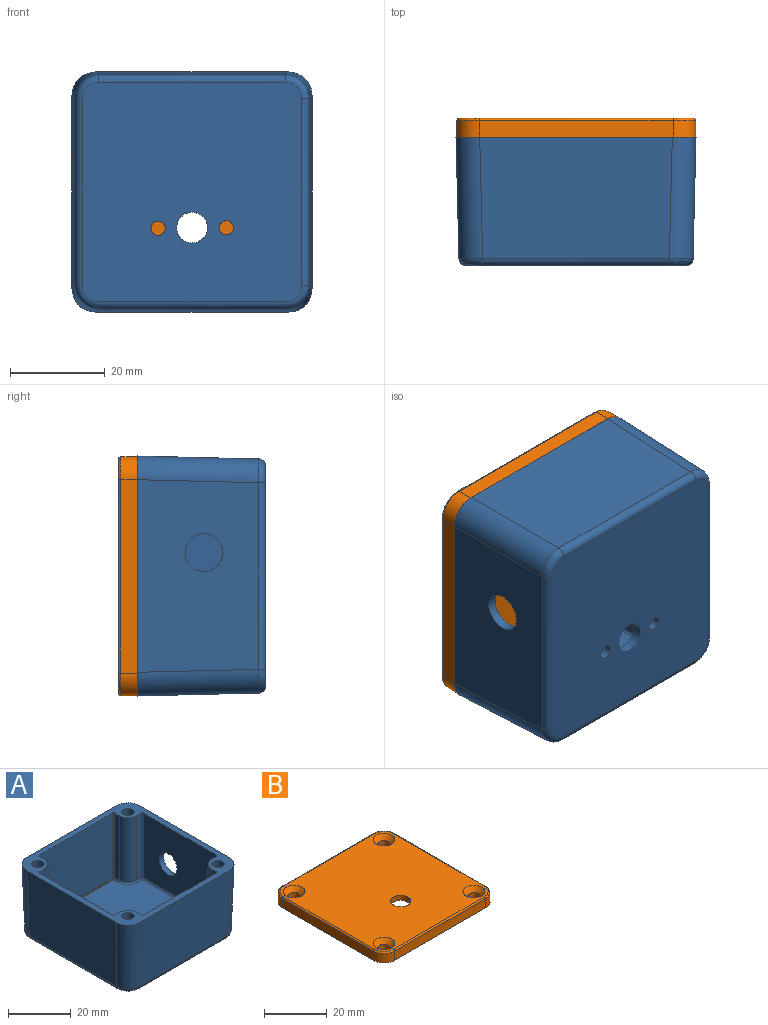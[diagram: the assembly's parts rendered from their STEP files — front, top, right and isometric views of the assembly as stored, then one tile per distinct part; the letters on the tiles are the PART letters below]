
ASSEMBLY  parts=2 mates=1
PART A: 289 faces, bbox 50.7x50.7x153.1 mm
  f0: plane 44.52x44.52mm, normal (0,0,1), area 1761.3mm2, adj f1,f69,f70,f71,f72,f73,f74,f75
  f1: cylinder r=1.5mm len=3mm, axis (0,0,1), area 18.4mm2, adj f0,f2
  f2: plane 46.36x46.36mm, normal (0,0,-1), area 2090.7mm2, adj f1,f3,f62,f63,f64,f65,f66,f67
  f3: bspline ~5x5mm, area 16.1mm2, adj f2,f4,f62,f68
  f4: cylinder r=5mm len=25.59mm, axis (-0.02,-0.02,-1), area 200.6mm2, adj f3,f5,f44,f61
  f5: plane 40.6x25.54mm, normal (1,0,-0.02), area 971mm2, adj f4,f6,f11,f44,f68
  f6: cylinder r=5mm len=25.59mm, axis (-0.02,0.02,-1), area 200.6mm2, adj f5,f7,f44,f67
  f7: plane 40.6x25.54mm, normal (0,-1,-0.02), area 1021.2mm2, adj f6,f8,f44,f66
  f8: cylinder r=5mm len=25.59mm, axis (0.02,0.02,-1), area 200.6mm2, adj f7,f9,f44,f65
  f9: plane 40.6x25.54mm, normal (-1,0,-0.02), area 1021.2mm2, adj f8,f10,f44,f64
  f10: cylinder r=5mm len=25.59mm, axis (0.02,-0.02,-1), area 200.6mm2, adj f9,f44,f61,f63
  f11: cylinder r=4mm len=8.05mm, axis (1,0,-0.02), area 49mm2, adj f5,f12
  f12: plane 32.7x24.56mm, normal (-1,0,0.02), area 739.5mm2, adj f11,f13,f42,f44,f85
  f13: cylinder r=0.5mm len=24.57mm, axis (-0.02,-0.02,-1), area 19.3mm2, adj f12,f14,f41,f44
  f14: plane 24.56x2.56mm, normal (0,-1,0.02), area 48.6mm2, adj f13,f15,f44,f84
  f15: cylinder r=4mm len=24.6mm, axis (-0.02,-0.02,-1), area 154.4mm2, adj f14,f16,f44,f83
  f16: plane 24.56x2.56mm, normal (-1,0,0.02), area 48.6mm2, adj f15,f17,f44,f82
  f17: cylinder r=0.5mm len=24.57mm, axis (0.02,0.02,1), area 19.3mm2, adj f16,f18,f40,f44
  f18: plane 32.7x24.56mm, normal (0,-1,0.02), area 789.7mm2, adj f17,f19,f44,f80
  f19: cylinder r=0.5mm len=24.57mm, axis (0.02,-0.02,-1), area 19.3mm2, adj f18,f20,f39,f44
  f20: plane 24.56x2.56mm, normal (1,0,0.02), area 48.6mm2, adj f19,f21,f44,f79
  f21: cylinder r=4mm len=24.6mm, axis (0.02,-0.02,-1), area 154.4mm2, adj f20,f22,f44,f78
  f22: plane 24.56x2.56mm, normal (0,-1,0.02), area 48.6mm2, adj f21,f23,f44,f77
  f23: cylinder r=0.5mm len=24.57mm, axis (-0.02,0.02,1), area 19.3mm2, adj f22,f24,f38,f44
  f24: plane 32.7x24.56mm, normal (1,0,0.02), area 789.7mm2, adj f23,f25,f44,f76
  f25: cylinder r=0.5mm len=24.57mm, axis (0.02,0.02,-1), area 19.3mm2, adj f24,f26,f37,f44
  f26: plane 24.56x2.56mm, normal (0,1,0.02), area 48.6mm2, adj f25,f27,f44,f75
  f27: cylinder r=4mm len=24.6mm, axis (0.02,0.02,-1), area 154.4mm2, adj f26,f28,f44,f74
  f28: plane 24.56x2.56mm, normal (1,0,0.02), area 48.6mm2, adj f27,f29,f44,f73
  f29: cylinder r=0.5mm len=24.57mm, axis (-0.02,-0.02,1), area 19.3mm2, adj f28,f30,f36,f44
  f30: plane 32.7x24.56mm, normal (0,1,0.02), area 789.7mm2, adj f29,f31,f44,f72
  f31: cylinder r=0.5mm len=24.57mm, axis (-0.02,0.02,-1), area 19.3mm2, adj f30,f32,f35,f44
  f32: plane 24.56x2.56mm, normal (-1,0,0.02), area 48.6mm2, adj f31,f33,f44,f71
  f33: cylinder r=4mm len=24.6mm, axis (-0.02,0.02,-1), area 154.4mm2, adj f32,f34,f44,f70
  f34: plane 24.56x2.56mm, normal (0,1,0.02), area 48.6mm2, adj f33,f42,f44,f69
  f35: sphere r=0.5mm, area 0.5mm2, adj f31,f71,f72
  f36: sphere r=0.5mm, area 0.4mm2, adj f29,f72,f73
  f37: sphere r=0.5mm, area 0.4mm2, adj f25,f75,f76
  f38: sphere r=0.5mm, area 0.5mm2, adj f23,f76,f77
  f39: sphere r=0.5mm, area 0.7mm2, adj f19,f79,f80
  f40: sphere r=0.5mm, area 0.1mm2, adj f17,f80,f82
  f41: sphere r=0.5mm, area 0.2mm2, adj f13,f84,f85
  f42: cylinder r=0.5mm len=24.57mm, axis (0.02,-0.02,1), area 19.3mm2, adj f12,f34,f43,f44
  f43: sphere r=0.5mm, area 0.4mm2, adj f42,f69,f85
  f44: plane 50.7x50.7mm, normal (0,0,1), area 466mm2, adj f4,f5,f6,f7,f8,f9,f10,f12
  f45: cylinder r=1.95mm len=3.9mm, axis (0,0,1), area 29.4mm2, adj f44,f46
  f46: plane 3.9x3.9mm, normal (0,0,1), area 6.5mm2, adj f45,f47
  f47: cylinder r=1.32mm len=7.6mm, axis (0,0,1), area 63.1mm2, adj f46,f48
  f48: plane 2.64x2.64mm, normal (0,0,1), area 5.5mm2, adj f47
  f49: cylinder r=1.95mm len=3.9mm, axis (0,0,1), area 29.4mm2, adj f44,f50
  f50: plane 3.9x3.9mm, normal (0,0,1), area 6.5mm2, adj f49,f51
  f51: cylinder r=1.32mm len=7.6mm, axis (0,0,1), area 63.1mm2, adj f50,f52
  f52: plane 2.64x2.64mm, normal (0,0,1), area 5.5mm2, adj f51
  f53: cylinder r=1.95mm len=3.9mm, axis (0,0,1), area 29.4mm2, adj f44,f54
  f54: plane 3.9x3.9mm, normal (0,0,1), area 6.5mm2, adj f53,f55
  f55: cylinder r=1.32mm len=7.6mm, axis (0,0,1), area 63.1mm2, adj f54,f56
  f56: plane 2.64x2.64mm, normal (0,0,1), area 5.5mm2, adj f55
  f57: cylinder r=1.95mm len=3.9mm, axis (0,0,1), area 29.4mm2, adj f44,f58
  f58: plane 3.9x3.9mm, normal (0,0,1), area 6.5mm2, adj f57,f59
  f59: cylinder r=1.32mm len=7.6mm, axis (0,0,1), area 63.1mm2, adj f58,f60
  f60: plane 2.64x2.64mm, normal (0,0,1), area 5.5mm2, adj f59
  f61: plane 40.6x25.54mm, normal (0,1,-0.02), area 1021.2mm2, adj f4,f10,f44,f62
  f62: cylinder r=1.5mm len=39.35mm, axis (-1,0,0), area 91.3mm2, adj f2,f3,f61,f63
  f63: bspline ~5x5mm, area 16.1mm2, adj f2,f10,f62,f64
  f64: cylinder r=1.5mm len=39.35mm, axis (0,-1,0), area 91.3mm2, adj f2,f9,f63,f65
  f65: bspline ~5x5mm, area 16.1mm2, adj f2,f8,f64,f66
  f66: cylinder r=1.5mm len=39.35mm, axis (1,0,0), area 91.3mm2, adj f2,f7,f65,f67
  f67: bspline ~5x5mm, area 16.1mm2, adj f2,f6,f66,f68
  f68: cylinder r=1.5mm len=39.35mm, axis (0,1,0), area 91.3mm2, adj f2,f3,f5,f67
  f69: cylinder r=0.5mm len=1.96mm, axis (1,0,0), area 1.5mm2, adj f0,f34,f43,f70
  f70: bspline ~4.5x4.5mm, area 5.1mm2, adj f0,f33,f69,f71
  f71: cylinder r=0.5mm len=1.96mm, axis (0,1,0), area 1.5mm2, adj f0,f32,f35,f70
  f72: cylinder r=0.5mm len=31.59mm, axis (-1,0,0), area 24.4mm2, adj f0,f30,f35,f36
  f73: cylinder r=0.5mm len=1.96mm, axis (0,-1,0), area 1.5mm2, adj f0,f28,f36,f74
  f74: bspline ~4.5x4.5mm, area 5.1mm2, adj f0,f27,f73,f75
  f75: cylinder r=0.5mm len=1.96mm, axis (1,0,0), area 1.5mm2, adj f0,f26,f37,f74
  f76: cylinder r=0.5mm len=31.59mm, axis (0,1,0), area 24.4mm2, adj f0,f24,f37,f38
  f77: cylinder r=0.5mm len=1.96mm, axis (-1,0,0), area 1.5mm2, adj f0,f22,f38,f78
  f78: bspline ~4.5x4.5mm, area 5.1mm2, adj f0,f21,f77,f79
  f79: cylinder r=0.5mm len=1.96mm, axis (0,-1,0), area 1.5mm2, adj f0,f20,f39,f78
  f80: cylinder r=0.5mm len=31.59mm, axis (1,0,0), area 24.4mm2, adj f0,f18,f39,f40,f81
  f81: sphere r=0.5mm, area 0mm2, adj f80,f82
  f82: cylinder r=0.5mm len=1.96mm, axis (0,1,0), area 1.5mm2, adj f0,f16,f40,f81,f83
  f83: bspline ~4.5x4.5mm, area 5.1mm2, adj f0,f15,f82,f84
  f84: cylinder r=0.5mm len=1.96mm, axis (-1,0,0), area 1.5mm2, adj f0,f14,f41,f83
  f85: cylinder r=0.5mm len=31.59mm, axis (0,-1,0), area 24.4mm2, adj f0,f12,f41,f43
  f86: plane 0.89x0.2mm, normal (0,1,0), area 0.2mm2, adj f0,f87,f88,f92
  f87: plane 2x1.16mm, normal (0,0,1), area 0.7mm2, adj f86,f88,f89,f90,f91,f92
  f88: plane 1.76x0.2mm, normal (1,0,0), area 0.4mm2, adj f0,f86,f87,f89
  f89: plane 0.27x0.2mm, normal (0,1,0), area 0.1mm2, adj f0,f87,f88,f90
  f90: plane 2x0.2mm, normal (-1,0,0), area 0.4mm2, adj f0,f87,f89,f91
  f91: plane 1.16x0.2mm, normal (0,-1,0), area 0.2mm2, adj f0,f87,f90,f92
  f92: plane 0.24x0.2mm, normal (1,0,0), area 0mm2, adj f0,f86,f87,f91
  f93: bspline ~152.98x1.04mm, area 0.3mm2, adj f0,f94,f104,f106
  f94: plane 2.08x1.28mm, normal (0,0,1), area 1.2mm2, adj f93,f95,f97,f98,f99,f100,f101,f102
  f95: bspline ~152.98x0.61mm, area 0.1mm2, adj f94,f96,f97,f103
  f96: plane 1.64x0.73mm, normal (0,0,1), area 1mm2, adj f95,f97,f98,f99,f100,f101,f102,f103
  f97: bspline ~152.98x0.61mm, area 0.1mm2, adj f94,f95,f96,f98
  f98: bspline ~152.98x0.29mm, area 0.1mm2, adj f94,f96,f97,f99
  f99: bspline ~152.98x0.3mm, area 0.1mm2, adj f94,f96,f98,f100
  f100: bspline ~152.98x0.61mm, area 0.1mm2, adj f94,f96,f99,f101
  f101: bspline ~152.98x0.6mm, area 0.1mm2, adj f94,f96,f100,f102
  f102: bspline ~152.98x0.3mm, area 0.1mm2, adj f94,f96,f101,f103
  f103: bspline ~152.98x0.3mm, area 0.1mm2, adj f94,f95,f96,f102
  f104: bspline ~152.98x1.04mm, area 0.3mm2, adj f0,f93,f94,f105
  f105: bspline ~152.98x1.04mm, area 0.3mm2, adj f0,f94,f104,f106
  f106: bspline ~152.98x1.04mm, area 0.3mm2, adj f0,f93,f94,f105
  f107: plane 0.2x0.01mm, normal (0,1,0), area 0mm2, adj f0,f108,f117,f129
  f108: plane 2.08x1.3mm, normal (0,0,1), area 1.2mm2, adj f107,f109,f111,f112,f113,f114,f115,f116
  f109: bspline ~152.98x0.53mm, area 0.1mm2, adj f108,f110,f111,f116
  f110: plane 0.88x0.75mm, normal (0,0,1), area 0.5mm2, adj f109,f111,f112,f113,f114,f115,f116
  f111: bspline ~152.98x0.25mm, area 0.1mm2, adj f108,f109,f110,f112
  f112: bspline ~152.98x0.46mm, area 0.1mm2, adj f108,f110,f111,f113
  f113: bspline ~152.98x0.35mm, area 0.1mm2, adj f108,f110,f112,f114
  f114: bspline ~152.98x0.25mm, area 0.1mm2, adj f108,f110,f113,f115
  f115: bspline ~152.98x0.36mm, area 0.1mm2, adj f108,f110,f114,f116
  f116: bspline ~152.98x0.13mm, area 0mm2, adj f108,f109,f110,f115
  f117: plane 0.26x0.2mm, normal (-1,0,0), area 0.1mm2, adj f0,f107,f108,f118
  f118: bspline ~152.98x0.23mm, area 0mm2, adj f0,f108,f117,f119
  f119: bspline ~152.98x0.68mm, area 0.2mm2, adj f0,f108,f118,f120
  f120: bspline ~152.98x0.84mm, area 0.2mm2, adj f0,f108,f119,f121
  f121: bspline ~152.98x0.74mm, area 0.2mm2, adj f0,f108,f120,f122
  f122: bspline ~152.98x0.44mm, area 0.1mm2, adj f0,f108,f121,f123
  f123: bspline ~152.98x0.45mm, area 0.1mm2, adj f0,f108,f122,f124
  f124: bspline ~152.98x0.5mm, area 0.1mm2, adj f0,f108,f123,f125
  f125: bspline ~152.98x0.51mm, area 0.1mm2, adj f0,f108,f124,f126
  f126: bspline ~152.98x0.39mm, area 0.1mm2, adj f0,f108,f125,f127
  f127: bspline ~152.98x0.42mm, area 0.1mm2, adj f0,f108,f126,f128
  f128: bspline ~152.98x0.67mm, area 0.2mm2, adj f0,f108,f127,f129
  f129: bspline ~152.98x0.25mm, area 0.1mm2, adj f0,f107,f108,f128
  f130: bspline ~152.98x0.4mm, area 0.1mm2, adj f0,f131,f132,f150
  f131: plane 2.04x1.19mm, normal (0,0,1), area 1.1mm2, adj f130,f132,f133,f134,f135,f136,f137,f138
  f132: bspline ~152.98x0.33mm, area 0.1mm2, adj f0,f130,f131,f133
  f133: bspline ~152.98x0.29mm, area 0.1mm2, adj f0,f131,f132,f134
  f134: bspline ~152.98x0.33mm, area 0.1mm2, adj f0,f131,f133,f135
  f135: bspline ~152.98x0.29mm, area 0.1mm2, adj f0,f131,f134,f136
  f136: bspline ~152.98x0.29mm, area 0.1mm2, adj f0,f131,f135,f137
  f137: bspline ~152.98x0.22mm, area 0mm2, adj f0,f131,f136,f138
  f138: plane 0.2x0.02mm, normal (0,1,0), area 0mm2, adj f0,f131,f137,f139
  f139: plane 0.28x0.2mm, normal (-1,0,0), area 0.1mm2, adj f0,f131,f138,f140
  f140: bspline ~152.98x0.52mm, area 0.1mm2, adj f0,f131,f139,f141
  f141: bspline ~152.98x0.49mm, area 0.1mm2, adj f0,f131,f140,f142
  f142: bspline ~152.98x0.48mm, area 0.1mm2, adj f0,f131,f141,f143
  f143: bspline ~152.98x0.48mm, area 0.1mm2, adj f0,f131,f142,f144
  f144: bspline ~152.98x0.46mm, area 0.1mm2, adj f0,f131,f143,f145
  f145: bspline ~152.98x0.18mm, area 0mm2, adj f0,f131,f144,f146
  f146: plane 0.53x0.2mm, normal (1,0,0), area 0.1mm2, adj f0,f131,f145,f147
  f147: plane 0.84x0.2mm, normal (0,-1,0), area 0.2mm2, adj f0,f131,f146,f148
  f148: plane 0.24x0.2mm, normal (1,0,0), area 0mm2, adj f0,f131,f147,f149
  f149: plane 1.1x0.2mm, normal (0,1,0), area 0.2mm2, adj f0,f131,f148,f150
  f150: plane 1.03x0.2mm, normal (-1,0,0), area 0.2mm2, adj f0,f130,f131,f149
  f151: bspline ~152.98x0.41mm, area 0.1mm2, adj f0,f152,f153,f162
  f152: plane 2.01x0.98mm, normal (0,0,1), area 0.7mm2, adj f151,f153,f154,f155,f156,f157,f158,f159
  f153: plane 0.2x0.18mm, normal (-1,0,0), area 0mm2, adj f0,f151,f152,f154
  f154: plane 0.36x0.2mm, normal (0,-1,0), area 0.1mm2, adj f0,f152,f153,f155
  f155: plane 1.34x0.2mm, normal (-1,0,0), area 0.3mm2, adj f0,f152,f154,f156
  f156: plane 0.36x0.2mm, normal (0,1,0), area 0.1mm2, adj f0,f152,f155,f157
  f157: plane 0.2x0.2mm, normal (-1,0,0), area 0mm2, adj f0,f152,f156,f158
  f158: plane 0.98x0.2mm, normal (0,-1,0), area 0.2mm2, adj f0,f152,f157,f159
  f159: plane 0.2x0.2mm, normal (1,0,0), area 0mm2, adj f0,f152,f158,f160
  f160: plane 0.36x0.2mm, normal (0,1,0), area 0.1mm2, adj f0,f152,f159,f161
  f161: plane 1.8x0.2mm, normal (1,0,0), area 0.4mm2, adj f0,f152,f160,f162
  f162: plane 0.21x0.2mm, normal (0,1,0), area 0mm2, adj f0,f151,f152,f161
  f163: plane 0.46x0.2mm, normal (0,1,0), area 0.1mm2, adj f0,f164,f173,f178
  f164: plane 2x1.58mm, normal (0,0,1), area 1.4mm2, adj f163,f165,f167,f168,f169,f170,f171,f172
  f165: bspline ~152.98x0.65mm, area 0.2mm2, adj f164,f166,f167,f172
  f166: plane 1.54x1.03mm, normal (0,0,1), area 1.4mm2, adj f165,f167,f168,f169,f170,f171,f172
  f167: bspline ~152.98x0.53mm, area 0.1mm2, adj f164,f165,f166,f168
  f168: plane 0.2x0.2mm, normal (0,-1,0), area 0mm2, adj f164,f166,f167,f169
  f169: plane 1.54x0.2mm, normal (1,0,0), area 0.3mm2, adj f164,f166,f168,f170
  f170: plane 0.2x0.2mm, normal (0,1,0), area 0mm2, adj f164,f166,f169,f171
  f171: bspline ~152.98x0.55mm, area 0.1mm2, adj f164,f166,f170,f172
  f172: bspline ~152.98x0.64mm, area 0.1mm2, adj f164,f165,f166,f171
  f173: plane 2x0.2mm, normal (-1,0,0), area 0.4mm2, adj f0,f163,f164,f174
  f174: plane 0.46x0.2mm, normal (0,-1,0), area 0.1mm2, adj f0,f164,f173,f175
  f175: bspline ~152.98x0.71mm, area 0.1mm2, adj f0,f164,f174,f176
  f176: bspline ~152.98x0.84mm, area 0.2mm2, adj f0,f164,f175,f177
  f177: bspline ~152.98x0.84mm, area 0.2mm2, adj f0,f164,f176,f178
  f178: bspline ~152.98x0.72mm, area 0.1mm2, adj f0,f163,f164,f177
  f179: plane 1.58x0.81mm, normal (0.89,0.45,0), area 0.4mm2, adj f0,f180,f181,f189
  f180: plane 2x1.43mm, normal (0,0,1), area 1.5mm2, adj f179,f181,f182,f183,f184,f185,f186,f187
  f181: plane 0.38x0.2mm, normal (0,1,0), area 0.1mm2, adj f0,f179,f180,f182
  f182: plane 2x0.2mm, normal (-1,0,0), area 0.4mm2, adj f0,f180,f181,f183
  f183: plane 0.25x0.2mm, normal (0,-1,0), area 0mm2, adj f0,f180,f182,f184
  f184: plane 1.72x0.2mm, normal (1,0,0), area 0.3mm2, adj f0,f180,f183,f185
  f185: plane 1.72x0.89mm, normal (-0.89,-0.46,0), area 0.4mm2, adj f0,f180,f184,f186
  f186: plane 0.3x0.2mm, normal (0,-1,0), area 0.1mm2, adj f0,f180,f185,f187
  f187: plane 2x0.2mm, normal (1,0,0), area 0.4mm2, adj f0,f180,f186,f188
  f188: plane 0.25x0.2mm, normal (0,1,0), area 0mm2, adj f0,f180,f187,f189
  f189: plane 1.58x0.2mm, normal (-1,0,0), area 0.3mm2, adj f0,f179,f180,f188
  f190: bspline ~152.98x0.77mm, area 0.2mm2, adj f0,f191,f199,f205
  f191: plane 2.08x1.77mm, normal (0,0,1), area 1.4mm2, adj f190,f192,f194,f195,f196,f197,f198,f199
  f192: bspline ~152.98x0.6mm, area 0.1mm2, adj f191,f193,f194,f198
  f193: plane 1.62x1.21mm, normal (0,0,1), area 1.6mm2, adj f192,f194,f195,f196,f197,f198
  f194: bspline ~152.98x0.44mm, area 0.1mm2, adj f191,f192,f193,f195
  f195: bspline ~152.98x0.44mm, area 0.1mm2, adj f191,f193,f194,f196
  f196: bspline ~152.98x0.6mm, area 0.1mm2, adj f191,f193,f195,f197
  f197: bspline ~152.98x0.81mm, area 0.2mm2, adj f191,f193,f196,f198
  f198: bspline ~152.98x0.81mm, area 0.2mm2, adj f191,f192,f193,f197
  f199: bspline ~152.98x0.77mm, area 0.2mm2, adj f0,f190,f191,f200
  f200: bspline ~152.98x0.65mm, area 0.1mm2, adj f0,f191,f199,f201
  f201: bspline ~152.98x0.65mm, area 0.1mm2, adj f0,f191,f200,f202
  f202: bspline ~152.98x0.77mm, area 0.2mm2, adj f0,f191,f201,f203
  f203: bspline ~152.98x0.77mm, area 0.2mm2, adj f0,f191,f202,f204
  f204: bspline ~152.98x0.65mm, area 0.1mm2, adj f0,f191,f203,f205
  f205: bspline ~152.98x0.64mm, area 0.1mm2, adj f0,f190,f191,f204
  f206: plane 2x0.2mm, normal (-1,0,0), area 0.4mm2, adj f0,f207,f208,f219
  f207: plane 2x1.71mm, normal (0,0,1), area 1.6mm2, adj f206,f208,f209,f210,f211,f212,f213,f214
  f208: plane 0.25x0.2mm, normal (0,-1,0), area 0mm2, adj f0,f206,f207,f209
  f209: plane 1.72x0.2mm, normal (1,0,0), area 0.3mm2, adj f0,f207,f208,f210
  f210: plane 1.17x0.52mm, normal (-0.91,-0.4,0), area 0.3mm2, adj f0,f207,f209,f211
  f211: plane 0.2x0.16mm, normal (0,-1,0), area 0mm2, adj f0,f207,f210,f212
  f212: plane 1.17x0.52mm, normal (0.91,-0.41,0), area 0.3mm2, adj f0,f207,f211,f213
  f213: plane 1.72x0.2mm, normal (-1,0,0), area 0.3mm2, adj f0,f207,f212,f214
  f214: plane 0.27x0.2mm, normal (0,-1,0), area 0.1mm2, adj f0,f207,f213,f215
  f215: plane 2x0.2mm, normal (1,0,0), area 0.4mm2, adj f0,f207,f214,f216
  f216: plane 0.37x0.2mm, normal (0,1,0), area 0.1mm2, adj f0,f207,f215,f217
  f217: plane 1.11x0.48mm, normal (-0.92,0.4,0), area 0.2mm2, adj f0,f207,f216,f218
  f218: plane 1.11x0.5mm, normal (0.91,0.41,0), area 0.2mm2, adj f0,f207,f217,f219
  f219: plane 0.36x0.2mm, normal (0,1,0), area 0.1mm2, adj f0,f206,f207,f218
  f220: plane 2x0.2mm, normal (-1,0,0), area 0.4mm2, adj f0,f221,f222,f233
  f221: plane 2x1.71mm, normal (0,0,1), area 1.6mm2, adj f220,f222,f223,f224,f225,f226,f227,f228
  f222: plane 0.25x0.2mm, normal (0,-1,0), area 0mm2, adj f0,f220,f221,f223
  f223: plane 1.72x0.2mm, normal (1,0,0), area 0.3mm2, adj f0,f221,f222,f224
  f224: plane 1.17x0.52mm, normal (-0.91,-0.4,0), area 0.3mm2, adj f0,f221,f223,f225
  f225: plane 0.2x0.16mm, normal (0,-1,0), area 0mm2, adj f0,f221,f224,f226
  f226: plane 1.17x0.52mm, normal (0.91,-0.41,0), area 0.3mm2, adj f0,f221,f225,f227
  f227: plane 1.72x0.2mm, normal (-1,0,0), area 0.3mm2, adj f0,f221,f226,f228
  f228: plane 0.27x0.2mm, normal (0,-1,0), area 0.1mm2, adj f0,f221,f227,f229
  f229: plane 2x0.2mm, normal (1,0,0), area 0.4mm2, adj f0,f221,f228,f230
  f230: plane 0.37x0.2mm, normal (0,1,0), area 0.1mm2, adj f0,f221,f229,f231
  f231: plane 1.11x0.48mm, normal (-0.92,0.4,0), area 0.2mm2, adj f0,f221,f230,f232
  f232: plane 1.11x0.5mm, normal (0.91,0.41,0), area 0.2mm2, adj f0,f221,f231,f233
  f233: plane 0.36x0.2mm, normal (0,1,0), area 0.1mm2, adj f0,f220,f221,f232
  f234: plane 0.76x0.2mm, normal (0,-1,0), area 0.2mm2, adj f0,f235,f240,f246
  f235: plane 2x1.68mm, normal (0,0,1), area 1.2mm2, adj f234,f236,f238,f239,f240,f241,f242,f243
  f236: plane 0.94x0.31mm, normal (-0.95,-0.31,0), area 0.2mm2, adj f235,f237,f238,f239
  f237: plane 0.94x0.62mm, normal (0,0,1), area 0.3mm2, adj f236,f238,f239
  f238: plane 0.94x0.31mm, normal (0.95,-0.31,0), area 0.2mm2, adj f235,f236,f237,f239
  f239: plane 0.62x0.2mm, normal (0,1,0), area 0.1mm2, adj f235,f236,f237,f238
  f240: plane 0.56x0.2mm, normal (-0.95,-0.31,0), area 0.1mm2, adj f0,f234,f235,f241
  f241: plane 0.28x0.2mm, normal (0,-1,0), area 0.1mm2, adj f0,f235,f240,f242
  f242: plane 2x0.67mm, normal (0.95,0.32,0), area 0.4mm2, adj f0,f235,f241,f243
  f243: plane 0.33x0.2mm, normal (0,1,0), area 0.1mm2, adj f0,f235,f242,f244
  f244: plane 2x0.67mm, normal (-0.95,0.32,0), area 0.4mm2, adj f0,f235,f243,f245
  f245: plane 0.27x0.2mm, normal (0,-1,0), area 0.1mm2, adj f0,f235,f244,f246
  f246: plane 0.56x0.2mm, normal (0.95,-0.31,0), area 0.1mm2, adj f0,f234,f235,f245
  f247: plane 0.78x0.2mm, normal (1,0,0), area 0.2mm2, adj f0,f248,f249,f259
  f248: plane 2x1.45mm, normal (0,0,1), area 1.3mm2, adj f247,f249,f250,f251,f252,f253,f254,f255
  f249: plane 0.27x0.2mm, normal (0,1,0), area 0.1mm2, adj f0,f247,f248,f250
  f250: plane 2x0.2mm, normal (-1,0,0), area 0.4mm2, adj f0,f248,f249,f251
  f251: plane 0.27x0.2mm, normal (0,-1,0), area 0.1mm2, adj f0,f248,f250,f252
  f252: plane 0.98x0.2mm, normal (1,0,0), area 0.2mm2, adj f0,f248,f251,f253
  f253: plane 0.92x0.2mm, normal (0,-1,0), area 0.2mm2, adj f0,f248,f252,f254
  f254: plane 0.98x0.2mm, normal (-1,0,0), area 0.2mm2, adj f0,f248,f253,f255
  f255: plane 0.27x0.2mm, normal (0,-1,0), area 0.1mm2, adj f0,f248,f254,f256
  f256: plane 2x0.2mm, normal (1,0,0), area 0.4mm2, adj f0,f248,f255,f257
  f257: plane 0.27x0.2mm, normal (0,1,0), area 0.1mm2, adj f0,f248,f256,f258
  f258: plane 0.78x0.2mm, normal (-1,0,0), area 0.2mm2, adj f0,f248,f257,f259
  f259: plane 0.92x0.2mm, normal (0,1,0), area 0.2mm2, adj f0,f247,f248,f258
  f260: bspline ~152.98x0.37mm, area 0.1mm2, adj f0,f261,f278,f286
  f261: plane 2x1.36mm, normal (0,0,1), area 1.5mm2, adj f260,f262,f264,f265,f266,f267,f268,f269
  f262: bspline ~152.98x0.31mm, area 0.1mm2, adj f261,f263,f264,f269
  f263: plane 0.81x0.74mm, normal (0,0,1), area 0.5mm2, adj f262,f264,f265,f266,f267,f268,f269
  f264: bspline ~152.98x0.35mm, area 0.1mm2, adj f261,f262,f263,f265
  f265: plane 0.3x0.2mm, normal (0,-1,0), area 0.1mm2, adj f261,f263,f264,f266
  f266: plane 0.74x0.2mm, normal (1,0,0), area 0.1mm2, adj f261,f263,f265,f267
  f267: plane 0.22x0.2mm, normal (0,1,0), area 0mm2, adj f261,f263,f266,f268
  f268: bspline ~152.98x0.45mm, area 0.1mm2, adj f261,f263,f267,f269
  f269: bspline ~152.98x0.29mm, area 0.1mm2, adj f261,f262,f263,f268
  f270: bspline ~152.98x0.21mm, area 0mm2, adj f261,f271,f272,f277
  f271: plane 0.72x0.59mm, normal (0,0,1), area 0.4mm2, adj f270,f272,f273,f274,f275,f276,f277
  f272: bspline ~152.98x0.36mm, area 0.1mm2, adj f261,f270,f271,f273
  f273: plane 0.25x0.2mm, normal (0,-1,0), area 0.1mm2, adj f261,f271,f272,f274
  f274: plane 0.59x0.2mm, normal (1,0,0), area 0.1mm2, adj f261,f271,f273,f275
  f275: plane 0.3x0.2mm, normal (0,1,0), area 0.1mm2, adj f261,f271,f274,f276
  f276: bspline ~152.98x0.31mm, area 0.1mm2, adj f261,f271,f275,f277
  f277: bspline ~152.98x0.26mm, area 0.1mm2, adj f261,f270,f271,f276
  f278: bspline ~152.98x0.53mm, area 0.1mm2, adj f0,f260,f261,f279
  f279: plane 0.53x0.2mm, normal (0,1,0), area 0.1mm2, adj f0,f261,f278,f280
  f280: plane 2x0.2mm, normal (-1,0,0), area 0.4mm2, adj f0,f261,f279,f281
  f281: plane 0.57x0.2mm, normal (0,-1,0), area 0.1mm2, adj f0,f261,f280,f282
  f282: bspline ~152.98x0.58mm, area 0.1mm2, adj f0,f261,f281,f283
  f283: bspline ~152.98x0.45mm, area 0.1mm2, adj f0,f261,f282,f284
  f284: bspline ~152.98x0.5mm, area 0.1mm2, adj f0,f261,f283,f285
  f285: plane 0.2x0.01mm, normal (1,0,0), area 0mm2, adj f0,f261,f284,f286
  f286: bspline ~152.98x0.43mm, area 0.1mm2, adj f0,f260,f261,f285
  f287: cylinder r=3.25mm len=6.5mm, axis (0,0,1), area 39.8mm2, adj f0,f2
  f288: cylinder r=1.5mm len=3mm, axis (0,0,1), area 18.4mm2, adj f0,f2
PART B: 77 faces, bbox 50.6x50.6x6.1 mm
  f0: cylinder r=0.4mm len=27.5mm, axis (-1,0,0), area 17mm2, adj f1,f15,f23,f24
  f1: torus R=0.62mm, axis (0,0,-1), area 0.8mm2, adj f0,f2,f22,f24
  f2: torus R=5.88mm, axis (0,0,1), area 5.5mm2, adj f1,f3,f21,f24
  f3: torus R=0.62mm, axis (0,0,-1), area 0.8mm2, adj f2,f4,f20,f24
  f4: cylinder r=0.4mm len=27.5mm, axis (0,1,0), area 17mm2, adj f3,f5,f19,f24
  f5: torus R=0.62mm, axis (0,0,-1), area 0.8mm2, adj f4,f6,f18,f24
  f6: torus R=5.88mm, axis (0,0,1), area 5.5mm2, adj f5,f7,f17,f24
  f7: torus R=0.62mm, axis (0,0,-1), area 0.8mm2, adj f6,f8,f16,f24
  f8: cylinder r=0.4mm len=27.5mm, axis (1,0,0), area 17mm2, adj f7,f9,f24,f55
  f9: torus R=0.62mm, axis (0,0,-1), area 0.8mm2, adj f8,f10,f24,f48
  f10: torus R=5.88mm, axis (0,0,1), area 5.5mm2, adj f9,f11,f24,f49
  f11: torus R=0.62mm, axis (0,0,-1), area 0.8mm2, adj f10,f12,f24,f50
  f12: cylinder r=0.4mm len=27.5mm, axis (0,-1,0), area 17mm2, adj f11,f13,f24,f51
  f13: torus R=0.62mm, axis (0,0,-1), area 0.8mm2, adj f12,f14,f24,f52
  f14: torus R=5.88mm, axis (0,0,1), area 5.5mm2, adj f13,f15,f24,f53
  f15: torus R=0.62mm, axis (0,0,-1), area 0.8mm2, adj f0,f14,f24,f54
  f16: cone r=1.1mm half-angle=1.3deg, axis (0,0,-1), area 6mm2, adj f7,f17,f55,f72
  f17: cone r=5.4mm half-angle=1.3deg, axis (0,0,1), area 30.9mm2, adj f6,f16,f18,f72
  f18: cone r=1.1mm half-angle=1.3deg, axis (0,0,-1), area 6mm2, adj f5,f17,f19,f72
  f19: plane 27.5x3.61mm, normal (1,0,-0.02), area 99.3mm2, adj f4,f18,f20,f72
  f20: cone r=1.1mm half-angle=1.3deg, axis (0,0,-1), area 6mm2, adj f3,f19,f21,f72
  f21: cone r=5.4mm half-angle=1.3deg, axis (0,0,1), area 30.9mm2, adj f2,f20,f22,f72
  f22: cone r=1.1mm half-angle=1.3deg, axis (0,0,-1), area 6mm2, adj f1,f21,f23,f72
  f23: plane 27.5x3.61mm, normal (0,1,-0.02), area 99.3mm2, adj f0,f22,f54,f72
  f24: plane 41.74x41.74mm, normal (0,0,-1), area 1568.8mm2, adj f0,f1,f2,f3,f4,f5,f6,f7
  f25: cone r=2.73mm half-angle=41deg, axis (0,0,1), area 40.5mm2, adj f26,f47
  f26: cylinder r=1.95mm len=3.9mm, axis (0,0,1), area 27.2mm2, adj f25,f75
  f27: cone r=2.73mm half-angle=41deg, axis (0,0,1), area 40.5mm2, adj f28,f47
  f28: cylinder r=1.95mm len=3.9mm, axis (0,0,1), area 27.2mm2, adj f27,f75
  f29: cone r=2.73mm half-angle=41deg, axis (0,0,1), area 40.5mm2, adj f30,f47
  f30: cylinder r=1.95mm len=3.9mm, axis (0,0,1), area 27.2mm2, adj f29,f75
  f31: cone r=2.73mm half-angle=41deg, axis (0,0,1), area 40.5mm2, adj f32,f47
  f32: cylinder r=1.95mm len=3.9mm, axis (0,0,1), area 27.2mm2, adj f31,f75
  f33: bspline ~4.75x4.75mm, area 5.5mm2, adj f34,f39,f44,f47
  f34: cylinder r=4.75mm len=4.83mm, axis (0.02,-0.02,1), area 26.2mm2, adj f33,f45,f74,f75
  f35: bspline ~4.75x4.75mm, area 5.5mm2, adj f36,f43,f44,f47
  f36: cylinder r=4.75mm len=4.83mm, axis (0.02,0.02,1), area 26.2mm2, adj f35,f73,f74,f75
  f37: bspline ~4.75x4.75mm, area 5.5mm2, adj f38,f39,f42,f47
  f38: cylinder r=4.75mm len=4.83mm, axis (-0.02,-0.02,1), area 26.2mm2, adj f37,f45,f46,f75
  f39: cylinder r=0.5mm len=40.84mm, axis (1,0,0), area 31.6mm2, adj f33,f37,f45,f47
  f40: bspline ~4.75x4.75mm, area 5.5mm2, adj f41,f42,f43,f47
  f41: cylinder r=4.75mm len=4.83mm, axis (-0.02,0.02,1), area 26.2mm2, adj f40,f46,f73,f75
  f42: cylinder r=0.5mm len=40.84mm, axis (0,-1,0), area 31.6mm2, adj f37,f40,f46,f47
  f43: cylinder r=0.5mm len=40.84mm, axis (-1,0,0), area 31.6mm2, adj f35,f40,f47,f73
  f44: cylinder r=0.5mm len=40.84mm, axis (0,1,0), area 31.6mm2, adj f33,f35,f47,f74
  f45: plane 41x3.51mm, normal (0,1,0.02), area 143.7mm2, adj f34,f38,f39,f75
  f46: plane 41x3.51mm, normal (1,0,0.02), area 143.7mm2, adj f38,f41,f42,f75
  f47: plane 49.36x49.36mm, normal (0,0,1), area 2231.8mm2, adj f25,f27,f29,f31,f33,f35,f37,f39
  f48: cone r=1.1mm half-angle=1.3deg, axis (0,0,-1), area 6mm2, adj f9,f49,f55,f72
  f49: cone r=5.4mm half-angle=1.3deg, axis (0,0,1), area 30.9mm2, adj f10,f48,f50,f72
  f50: cone r=1.1mm half-angle=1.3deg, axis (0,0,-1), area 6mm2, adj f11,f49,f51,f72
  f51: plane 27.5x3.61mm, normal (-1,0,-0.02), area 99.3mm2, adj f12,f50,f52,f72
  f52: cone r=1.1mm half-angle=1.3deg, axis (0,0,-1), area 6mm2, adj f13,f51,f53,f72
  f53: cone r=5.4mm half-angle=1.3deg, axis (0,0,1), area 30.9mm2, adj f14,f52,f54,f72
  f54: cone r=1.1mm half-angle=1.3deg, axis (0,0,-1), area 6mm2, adj f15,f23,f53,f72
  f55: plane 27.5x3.61mm, normal (0,-1,-0.02), area 99.3mm2, adj f8,f16,f48,f72
  f56: cone r=4mm half-angle=1.3deg, axis (0,0,-1), area 12.6mm2, adj f57,f71,f72,f75
  f57: cone r=2.5mm half-angle=1.3deg, axis (0,0,1), area 7.8mm2, adj f56,f58,f72,f75
  f58: plane 27.5x2mm, normal (0,1,-0.02), area 55mm2, adj f57,f59,f72,f75
  f59: cone r=2.5mm half-angle=1.3deg, axis (0,0,1), area 7.8mm2, adj f58,f60,f72,f75
  f60: cone r=4mm half-angle=1.3deg, axis (0,0,-1), area 12.6mm2, adj f59,f61,f72,f75
  f61: cone r=2.5mm half-angle=1.3deg, axis (0,0,1), area 7.8mm2, adj f60,f62,f72,f75
  f62: plane 27.5x2mm, normal (-1,0,-0.02), area 55mm2, adj f61,f63,f72,f75
  f63: cone r=2.5mm half-angle=1.3deg, axis (0,0,1), area 7.8mm2, adj f62,f64,f72,f75
  f64: cone r=4mm half-angle=1.3deg, axis (0,0,-1), area 12.6mm2, adj f63,f65,f72,f75
  f65: cone r=2.5mm half-angle=1.3deg, axis (0,0,1), area 7.8mm2, adj f64,f66,f72,f75
  f66: plane 27.5x2mm, normal (0,-1,-0.02), area 55mm2, adj f65,f67,f72,f75
  f67: cone r=2.5mm half-angle=1.3deg, axis (0,0,1), area 7.8mm2, adj f66,f68,f72,f75
  f68: cone r=4mm half-angle=1.3deg, axis (0,0,-1), area 12.6mm2, adj f67,f69,f72,f75
  f69: cone r=2.5mm half-angle=1.3deg, axis (0,0,1), area 7.8mm2, adj f68,f70,f72,f75
  f70: plane 27.5x2mm, normal (1,0,-0.02), area 55mm2, adj f69,f71,f72,f75
  f71: cone r=2.5mm half-angle=1.3deg, axis (0,0,1), area 7.8mm2, adj f56,f70,f72,f75
  f72: plane 45.41x45.41mm, normal (0,0,-1), area 219.5mm2, adj f16,f17,f18,f19,f20,f21,f22,f23
  f73: plane 41x3.51mm, normal (0,-1,0.02), area 143.7mm2, adj f36,f41,f43,f75
  f74: plane 41x3.51mm, normal (-1,0,0.02), area 143.7mm2, adj f34,f36,f44,f75
  f75: plane 50.59x50.59mm, normal (0,0,-1), area 578.9mm2, adj f26,f28,f30,f32,f34,f36,f38,f41
  f76: cylinder r=3.25mm len=6.5mm, axis (0,0,1), area 40.8mm2, adj f24,f47
PLACE A rot(axis=(0,0.71,0.71),180deg) t=(29.93,5.42,5)mm
PLACE B rot(axis=(0,0.71,0.71),180deg) t=(29.98,5.42,4.95)mm
MATE fastened A.f44 <-> B.f2  axis (0,1,0) through (50.23,5.42,-15.3)mm
